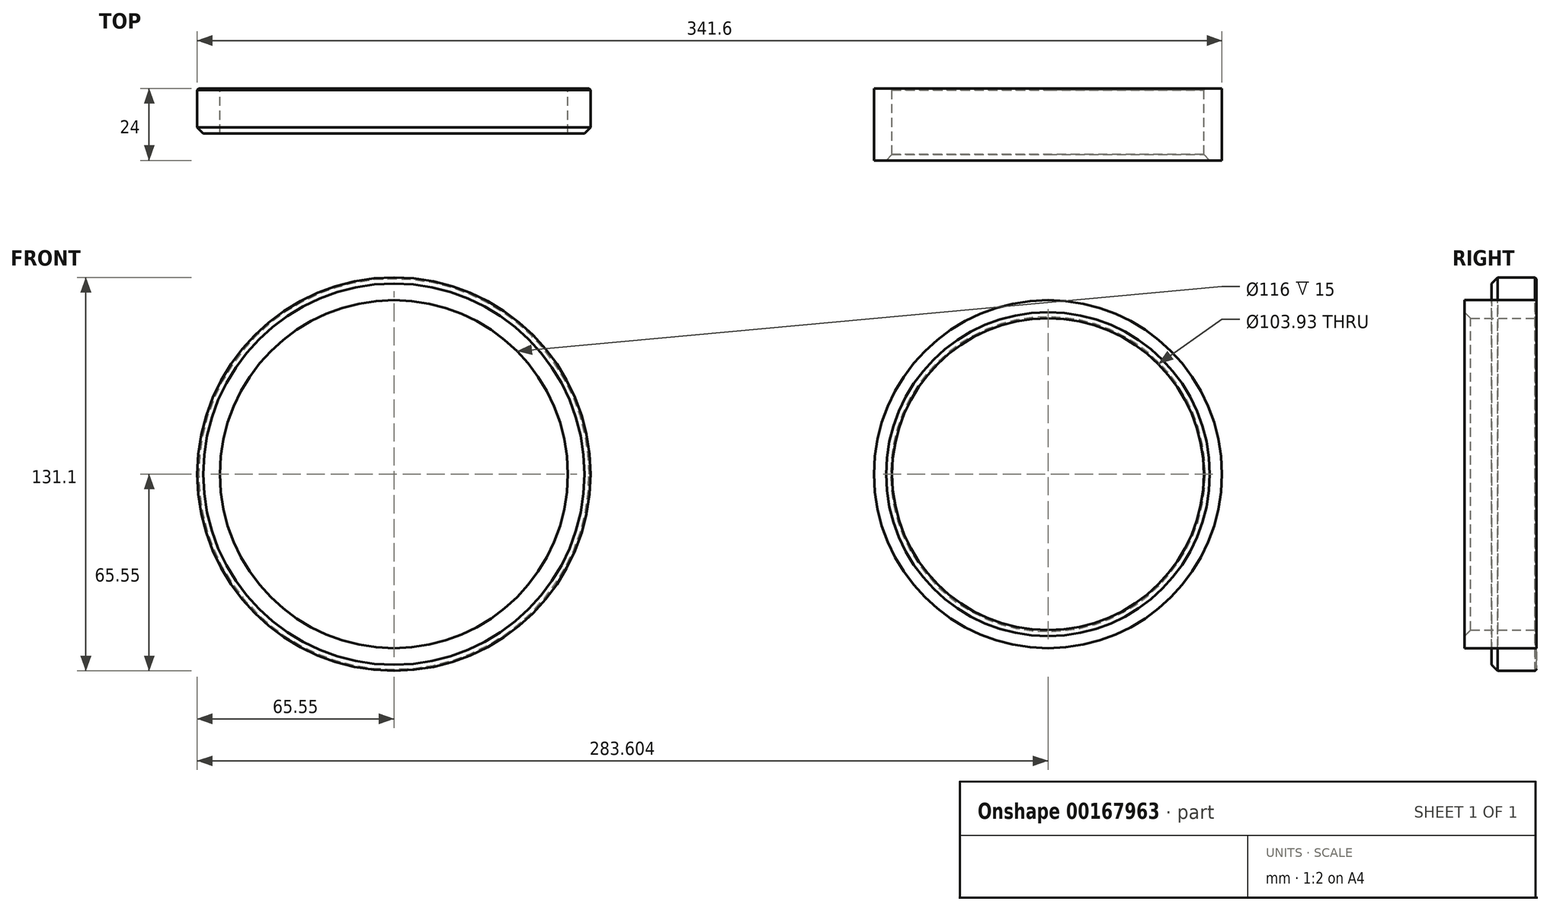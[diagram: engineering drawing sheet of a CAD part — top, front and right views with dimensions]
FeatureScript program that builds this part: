
annotation { "Feature Type Name" : "Feature", "Feature Type Description" : "" }
export const myFeature = defineFeature(function(context is Context, id is Id, definition is map)
    precondition{}
    {
        {
            var Q0;
            Q0=qCreatedBy(makeId("Front.planeOp"),FACE);
            var sketch = newSketch(context, id + "F0", { "sketchPlane" : qUnion([Q0])});
            skCircle(sketch, "E0", {"center": v(0, 0) * mm, "radius": 58 * mm});
            skCircle(sketch, "E1", {"center": v(0, 0) * mm, "radius": 65.55 * mm});
            skSolve(sketch);
        }
        {
            var Q0;
            Q0=qCreatedBy(makeId("Front.planeOp"),FACE);
            var sketch = newSketch(context, id + "F1", { "sketchPlane" : qUnion([Q0])});
            skCircle(sketch, "E2", {"center": v(218.05, 0) * mm, "radius": 58 * mm});
            skCircle(sketch, "E3", {"center": v(218.05, 0) * mm, "radius": 51.97 * mm});
            skSolve(sketch);
        }
        {
            var Q0;
            Q0 = qSketchRegion(id + "F1", true);
            extrude(context, id + "F2", {"entities" : qUnion([Q0]), "depth" : 24 * mm, "offsetDistance" : 25 * mm});
        }
        {
            var Q0;
            Q0=makeQuery(id+"F2.opExtrude","CAP_EDGE",EDGE,{"disambiguationData":[OSD([sQuery(id+"F1.wireOp",EDGE,"E3")])],"isStart":false});
            chamfer(context, id + "F3", {"entities" : qUnion([Q0]), "width" : 2 * mm, "tangentPropagation" : true});
        }
        {
            var Q0;
            Q0=makeQuery(id+"F2.opExtrude","CAP_EDGE",EDGE,{"disambiguationData":[OSD([sQuery(id+"F1.wireOp",EDGE,"E3")])],"isStart":true});
            chamfer(context, id + "F4", {"entities" : qUnion([Q0]), "width" : .5 * mm, "tangentPropagation" : true});
        }
        {
            var Q0;
            Q0=makeQuery(id+"F0.imprint","IMPRINT",FACE,{"disambiguationData":[TD([[makeQuery(id+"F0.imprint","IMPRINT",EDGE,{"derivedFrom":sQuery(id+"F0.wireOp",EDGE,"E0")}),-1.0]])]});
            extrude(context, id + "F5", {"entities" : qUnion([Q0]), "depth" : 15 * mm, "offsetDistance" : 25 * mm});
        }
        {
            var Q0;
            Q0=makeQuery(id+"F5.opExtrude","CAP_EDGE",EDGE,{"disambiguationData":[OSD([sQuery(id+"F0.wireOp",EDGE,"E1")])],"isStart":false});
            chamfer(context, id + "F6", {"entities" : qUnion([Q0]), "width" : 2 * mm, "tangentPropagation" : true});
        }
        {
            var Q0;
            Q0=makeQuery(id+"F5.opExtrude","CAP_EDGE",EDGE,{"disambiguationData":[OSD([sQuery(id+"F0.wireOp",EDGE,"E1")])],"isStart":true});
            chamfer(context, id + "F7", {"entities" : qUnion([Q0]), "width" : .5 * mm, "tangentPropagation" : true});
        }
    });
